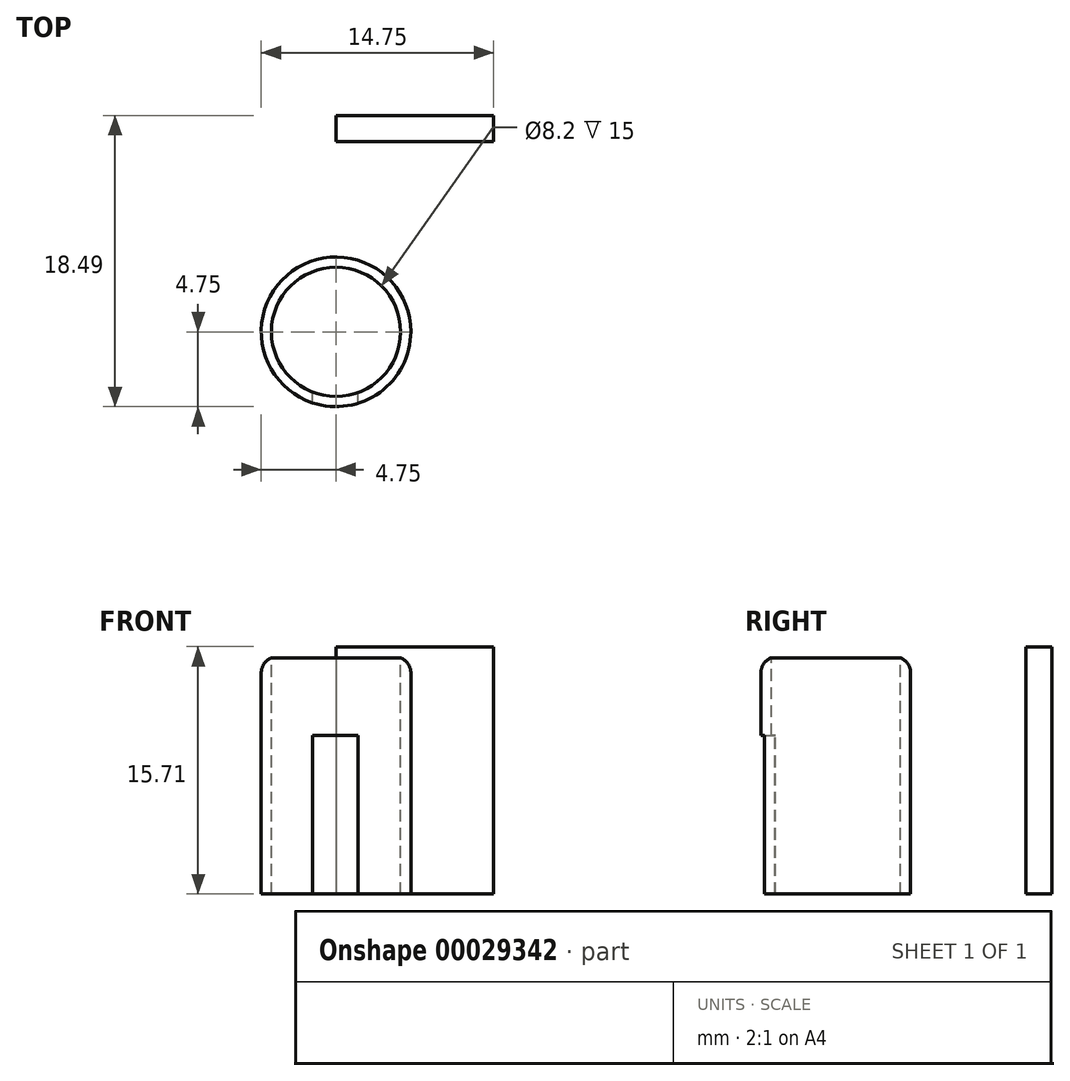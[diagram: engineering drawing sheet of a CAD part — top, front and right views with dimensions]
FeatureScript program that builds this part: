
annotation { "Feature Type Name" : "Feature", "Feature Type Description" : "" }
export const myFeature = defineFeature(function(context is Context, id is Id, definition is map)
    precondition{}
    {
        {
            var Q0;
            Q0=qCreatedBy(makeId("Top.planeOp"),FACE);
            var sketch = newSketch(context, id + "F0", { "sketchPlane" : qUnion([Q0])});
            skCircle(sketch, "E0", {"center": v(0, 0) * mm, "radius": 4.75 * mm});
            skSolve(sketch);
        }
        {
            var Q0;
            Q0 = qSketchRegion(id + "F0", true);
            extrude(context, id + "F1", {"entities" : qUnion([Q0]), "depth" : 15 * mm});
        }
        {
            var Q0;
            Q0=makeQuery(id+"F1.opExtrude","CAP_FACE",FACE,{"disambiguationData":[OSD([sQuery(id+"F0.wireOp",EDGE,"E0")])],"isStart":false});
            var sketch = newSketch(context, id + "F2", { "sketchPlane" : qUnion([Q0])});
            skCircle(sketch, "E1", {"center": v(0, 0) * mm, "radius": 4.1 * mm});
            skSolve(sketch);
        }
        {
            var Q0;
            Q0=makeQuery(id+"F2.imprint","IMPRINT",FACE,{"disambiguationData":[TD([[makeQuery(id+"F2.imprint","IMPRINT",EDGE,{"derivedFrom":sQuery(id+"F2.wireOp",EDGE,"E1")}),1.0]])]});
            extrude(context, id + "F3", {"entities" : qUnion([Q0]), "operationType" : NewBodyOperationType.REMOVE, "oppositeDirection" : true, "depth" : 25 * mm});
        }
        {
            var Q0;
            Q0=makeQuery(id+"F1.opExtrude","CAP_EDGE",EDGE,{"disambiguationData":[OSD([sQuery(id+"F0.wireOp",EDGE,"E0")])],"isStart":false});
            fillet(context, id + "F4", {"entities" : qUnion([Q0]), "radius" : 1 * mm, "tangentPropagation" : true, "allowEdgeOverflow" : false});
        }
        {
            var Q0;
            Q0=qCreatedBy(makeId("Front.planeOp"),FACE);
            var sketch = newSketch(context, id + "F5", { "sketchPlane" : qUnion([Q0])});
            skLineSegment(sketch, "E2.bottom", {"start": v(-1.48, 10.08) * mm, "end": v(1.4, 10.08) * mm});
            skLineSegment(sketch, "E2.top", {"start": v(-1.48, -0.58) * mm, "end": v(1.4, -0.58) * mm});
            skLineSegment(sketch, "E2.left", {"start": v(-1.48, 10.08) * mm, "end": v(-1.48, -0.58) * mm});
            skLineSegment(sketch, "E2.right", {"start": v(1.4, 10.08) * mm, "end": v(1.4, -0.58) * mm});
            skSolve(sketch);
        }
        {
            var Q0;
            Q0 = qSketchRegion(id + "F5", true);
            extrude(context, id + "F6", {"entities" : qUnion([Q0]), "operationType" : NewBodyOperationType.REMOVE, "depth" : 25 * mm});
        }
        {
            var Q0;
            Q0=qCreatedBy(makeId("Right.planeOp"),FACE);
            var sketch = newSketch(context, id + "F7", { "sketchPlane" : qUnion([Q0])});
            skLineSegment(sketch, "E3.bottom", {"start": v(12.07, 15.7) * mm, "end": v(13.74, 15.7) * mm});
            skLineSegment(sketch, "E3.top", {"start": v(12.07, 0) * mm, "end": v(13.74, 0) * mm});
            skLineSegment(sketch, "E3.left", {"start": v(12.07, 15.7) * mm, "end": v(12.07, 0) * mm});
            skLineSegment(sketch, "E3.right", {"start": v(13.74, 15.7) * mm, "end": v(13.74, 0) * mm});
            skSolve(sketch);
        }
        {
            var Q0;
            Q0=makeQuery(id+"F7.imprint","IMPRINT",FACE,{"disambiguationData":[TD([[makeQuery(id+"F7.imprint","IMPRINT",EDGE,{"derivedFrom":sQuery(id+"F7.wireOp",EDGE,"E3.bottom")}),-1.0]])]});
            extrude(context, id + "F8", {"entities" : qUnion([Q0]), "depth" : 10 * mm});
        }
    });
